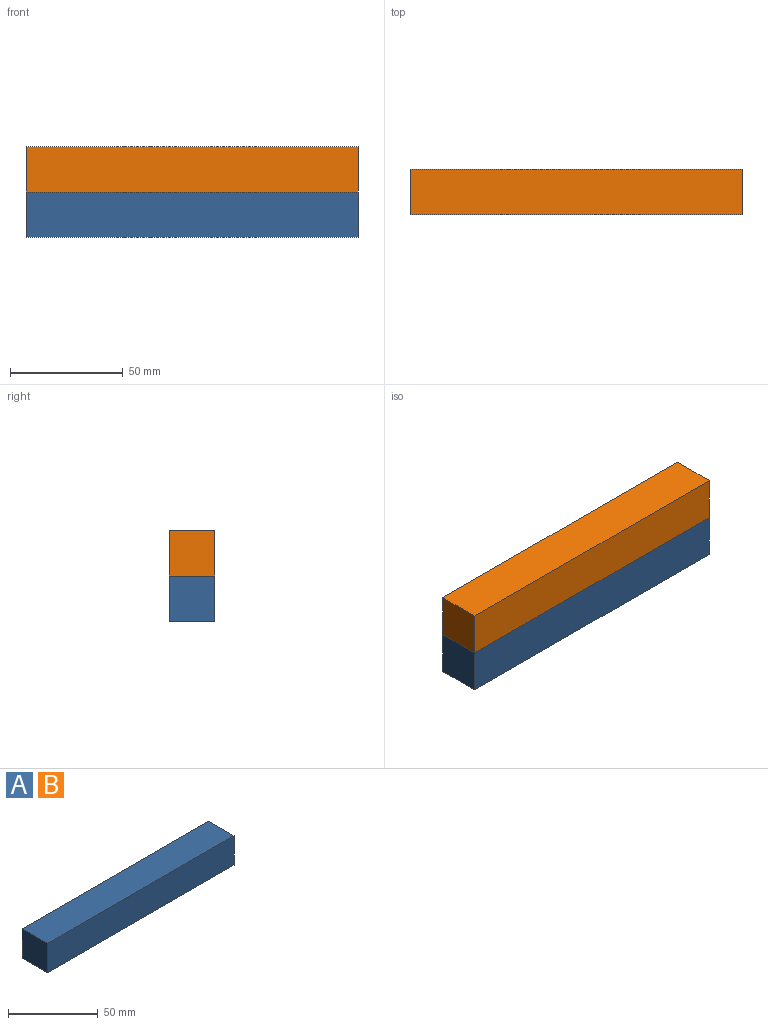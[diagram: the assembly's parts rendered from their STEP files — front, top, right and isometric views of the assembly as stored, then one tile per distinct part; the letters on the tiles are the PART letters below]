
ASSEMBLY  parts=2 mates=1
PART A: 6 faces, bbox 147x20x20 mm
  f0: plane 147x20mm, normal (0,1,0), area 2940mm2, adj f1,f3,f4,f5
  f1: plane 20x20mm, normal (-1,0,0), area 400mm2, adj f0,f2,f4,f5
  f2: plane 147x20mm, normal (0,-1,0), area 2940mm2, adj f1,f3,f4,f5
  f3: plane 20x20mm, normal (1,0,0), area 400mm2, adj f0,f2,f4,f5
  f4: plane 147x20mm, normal (0,0,1), area 2940mm2, adj f0,f1,f2,f3
  f5: plane 147x20mm, normal (0,0,-1), area 2940mm2, adj f0,f1,f2,f3
PART B: same geometry as A
PLACE A t=(-46.45,-0.07,2.14)mm
PLACE B t=(-46.45,-0.07,22.14)mm
MATE fastened A.f4 <-> B.f5  axis (0,0,1) through (-46.45,-0.07,22.14)mm
